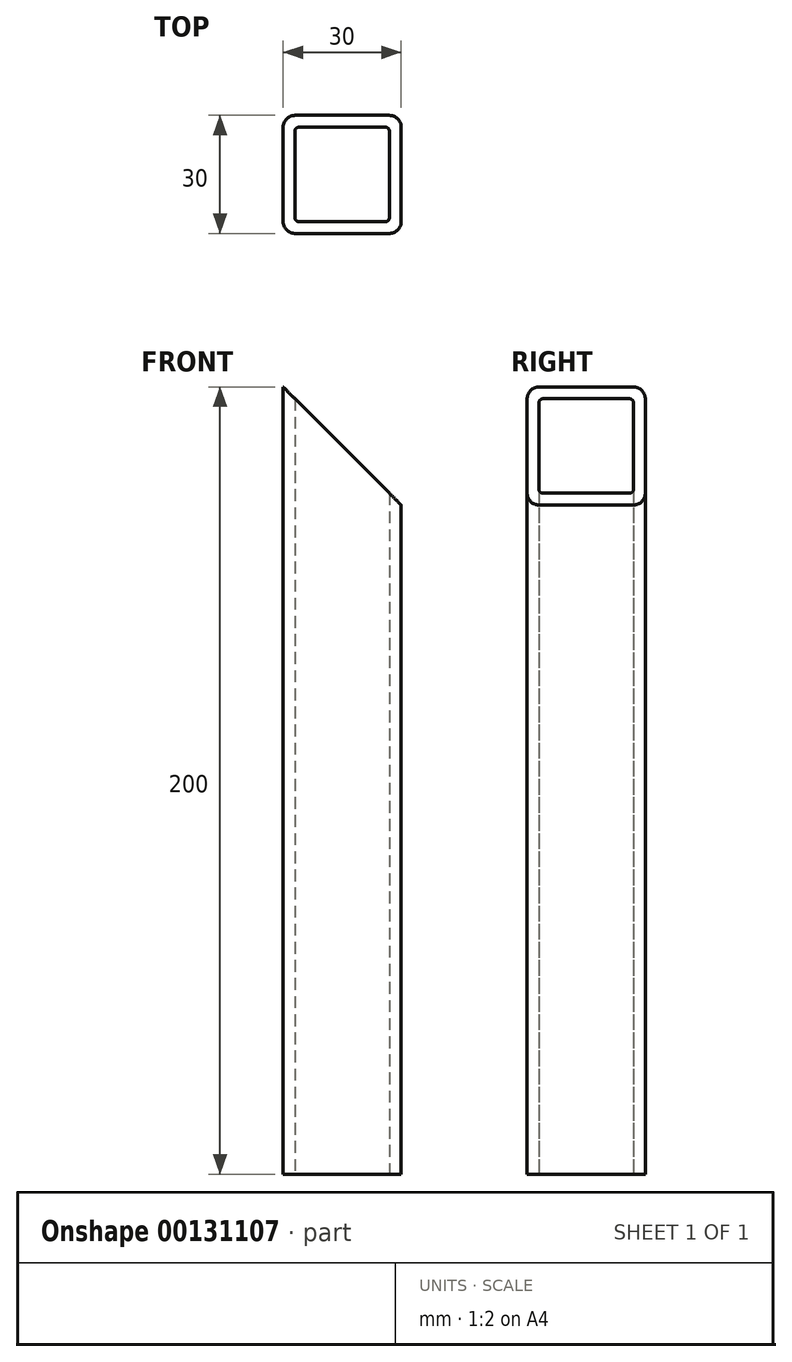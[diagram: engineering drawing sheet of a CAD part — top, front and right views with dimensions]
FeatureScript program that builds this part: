
annotation { "Feature Type Name" : "Feature", "Feature Type Description" : "" }
export const myFeature = defineFeature(function(context is Context, id is Id, definition is map)
    precondition{}
    {
        {
            var Q0;
            Q0=qCreatedBy(makeId("Top.planeOp"),FACE);
            var sketch = newSketch(context, id + "F0", { "sketchPlane" : qUnion([Q0])});
            skLineSegment(sketch, "E0.bottom", {"start": v(15, -15) * mm, "end": v(-15, -15) * mm});
            skLineSegment(sketch, "E0.top", {"start": v(15, 15) * mm, "end": v(-15, 15) * mm});
            skLineSegment(sketch, "E0.left", {"start": v(15, -15) * mm, "end": v(15, 15) * mm});
            skLineSegment(sketch, "E0.right", {"start": v(-15, -15) * mm, "end": v(-15, 15) * mm});
            skPoint(sketch, "E0.middle", {"position": v(0, 0) * mm});
            skLineSegment(sketch, "E1.bottom", {"start": v(12, -12) * mm, "end": v(-12, -12) * mm});
            skLineSegment(sketch, "E1.top", {"start": v(12, 12) * mm, "end": v(-12, 12) * mm});
            skLineSegment(sketch, "E1.left", {"start": v(12, -12) * mm, "end": v(12, 12) * mm});
            skLineSegment(sketch, "E1.right", {"start": v(-12, -12) * mm, "end": v(-12, 12) * mm});
            skSolve(sketch);
        }
        {
            var Q0;
            Q0=makeQuery(id+"F0.imprint","IMPRINT",FACE,{"disambiguationData":[TD([[makeQuery(id+"F0.imprint","IMPRINT",EDGE,{"derivedFrom":sQuery(id+"F0.wireOp",EDGE,"E0.bottom")}),-1.0]])]});
            extrude(context, id + "F1", {"entities" : qUnion([Q0]), "depth" : 200 * mm});
        }
        {
            var Q0;
            Q0=makeQuery(id+"F1.opExtrude","SWEPT_EDGE",EDGE,{"disambiguationData":[OSD([sQuery(id+"F0.wireOp",EDGE,"E1.bottom"),sQuery(id+"F0.wireOp",EDGE,"E1.right")])]});
            var Q1;
            Q1=makeQuery(id+"F1.opExtrude","SWEPT_EDGE",EDGE,{"disambiguationData":[OSD([sQuery(id+"F0.wireOp",EDGE,"E1.top"),sQuery(id+"F0.wireOp",EDGE,"E1.right")])]});
            var Q2;
            Q2=makeQuery(id+"F1.opExtrude","SWEPT_EDGE",EDGE,{"disambiguationData":[OSD([sQuery(id+"F0.wireOp",EDGE,"E1.top"),sQuery(id+"F0.wireOp",EDGE,"E1.left")])]});
            var Q3;
            Q3=makeQuery(id+"F1.opExtrude","SWEPT_EDGE",EDGE,{"disambiguationData":[OSD([sQuery(id+"F0.wireOp",EDGE,"E1.bottom"),sQuery(id+"F0.wireOp",EDGE,"E1.left")])]});
            fillet(context, id + "F2", {"entities" : qUnion([Q0, Q1, Q2, Q3]), "radius" : 1 * mm, "tangentPropagation" : true, "allowEdgeOverflow" : false});
        }
        {
            var Q0;
            Q0=makeQuery(id+"F1.opExtrude","SWEPT_EDGE",EDGE,{"disambiguationData":[OSD([sQuery(id+"F0.wireOp",EDGE,"E0.top"),sQuery(id+"F0.wireOp",EDGE,"E0.right")])]});
            var Q1;
            Q1=makeQuery(id+"F1.opExtrude","SWEPT_EDGE",EDGE,{"disambiguationData":[OSD([sQuery(id+"F0.wireOp",EDGE,"E0.bottom"),sQuery(id+"F0.wireOp",EDGE,"E0.right")])]});
            var Q2;
            Q2=makeQuery(id+"F1.opExtrude","SWEPT_EDGE",EDGE,{"disambiguationData":[OSD([sQuery(id+"F0.wireOp",EDGE,"E0.top"),sQuery(id+"F0.wireOp",EDGE,"E0.left")])]});
            var Q3;
            Q3=makeQuery(id+"F1.opExtrude","SWEPT_EDGE",EDGE,{"disambiguationData":[OSD([sQuery(id+"F0.wireOp",EDGE,"E0.bottom"),sQuery(id+"F0.wireOp",EDGE,"E0.left")])]});
            fillet(context, id + "F3", {"entities" : qUnion([Q0, Q1, Q2, Q3]), "radius" : 3 * mm, "tangentPropagation" : true, "allowEdgeOverflow" : false});
        }
        {
            var Q0;
            Q0=makeQuery(id+"F1.opExtrude","SWEPT_FACE",FACE,{"disambiguationData":[OSD([sQuery(id+"F0.wireOp",EDGE,"E0.bottom")])]});
            var sketch = newSketch(context, id + "F4", { "sketchPlane" : qUnion([Q0])});
            skLineSegment(sketch, "E2", {"start": v(-15, 200) * mm, "end": v(15, 170) * mm});
            skPoint(sketch, "E2.startSnap0", {"position": v(0, 200) * mm});
            skLineSegment(sketch, "E3", {"start": v(15, 170) * mm, "end": v(15, 200) * mm});
            skLineSegment(sketch, "E4", {"start": v(-15, 200) * mm, "end": v(15, 200) * mm});
            skSolve(sketch);
        }
        {
            var Q0;
            {var subQ0=sQuery(id+"F4.wireOp",EDGE,"E2");var subQ1=sQuery(id+"F0.wireOp",EDGE,"E0.bottom");var subQ2=makeQuery(id+"F1.opExtrude","SWEPT_FACE",FACE,{"disambiguationData":[OSD([subQ1])]});var subQ3=makeQuery(id+"F3.opFillet","BLEND_EDGE",EDGE,{"blendedFrom":[makeQuery(id+"F1.opExtrude","SWEPT_EDGE",EDGE,{"disambiguationData":[OSD([subQ1,sQuery(id+"F0.wireOp",EDGE,"E0.right")])]}),subQ2],"blendedInto":[subQ2]});var subQ4=makeQuery(id+"F4.imprint","INTERSECT",VERTEX,{"derivedFrom":[subQ3,subQ0]});Q0=makeQuery(id+"F4.imprint","IMPRINT",FACE,{"disambiguationData":[TD([[makeQuery(id+"F4.imprint","IMPRINT",EDGE,{"disambiguationData":[TD([[subQ4,-1.0]])],"derivedFrom":subQ0}),1.0]])]});}
            var Q1;
            {var subQ0=sQuery(id+"F4.wireOp",EDGE,"E4");var subQ1=sQuery(id+"F4.wireOp",EDGE,"E2");var subQ2=makeQuery(id+"F4.imprint","INTERSECT",VERTEX,{"derivedFrom":[subQ1,subQ0]});Q1=makeQuery(id+"F4.imprint","IMPRINT",FACE,{"disambiguationData":[TD([[makeQuery(id+"F4.imprint","IMPRINT",EDGE,{"disambiguationData":[TD([[subQ2,-1.0]])],"derivedFrom":subQ1}),1.0]])]});}
            var Q2;
            {var subQ0=sQuery(id+"F4.wireOp",EDGE,"E3");Q2=makeQuery(id+"F4.imprint","IMPRINT",FACE,{"disambiguationData":[TD([[makeQuery(id+"F4.imprint","IMPRINT",EDGE,{"derivedFrom":subQ0}),1.0]])]});}
            extrude(context, id + "F5", {"entities" : qUnion([Q0, Q1, Q2]), "operationType" : NewBodyOperationType.REMOVE, "endBound" : BoundingType.THROUGH_ALL, "oppositeDirection" : true, "depth" : 25 * mm});
        }
    });
